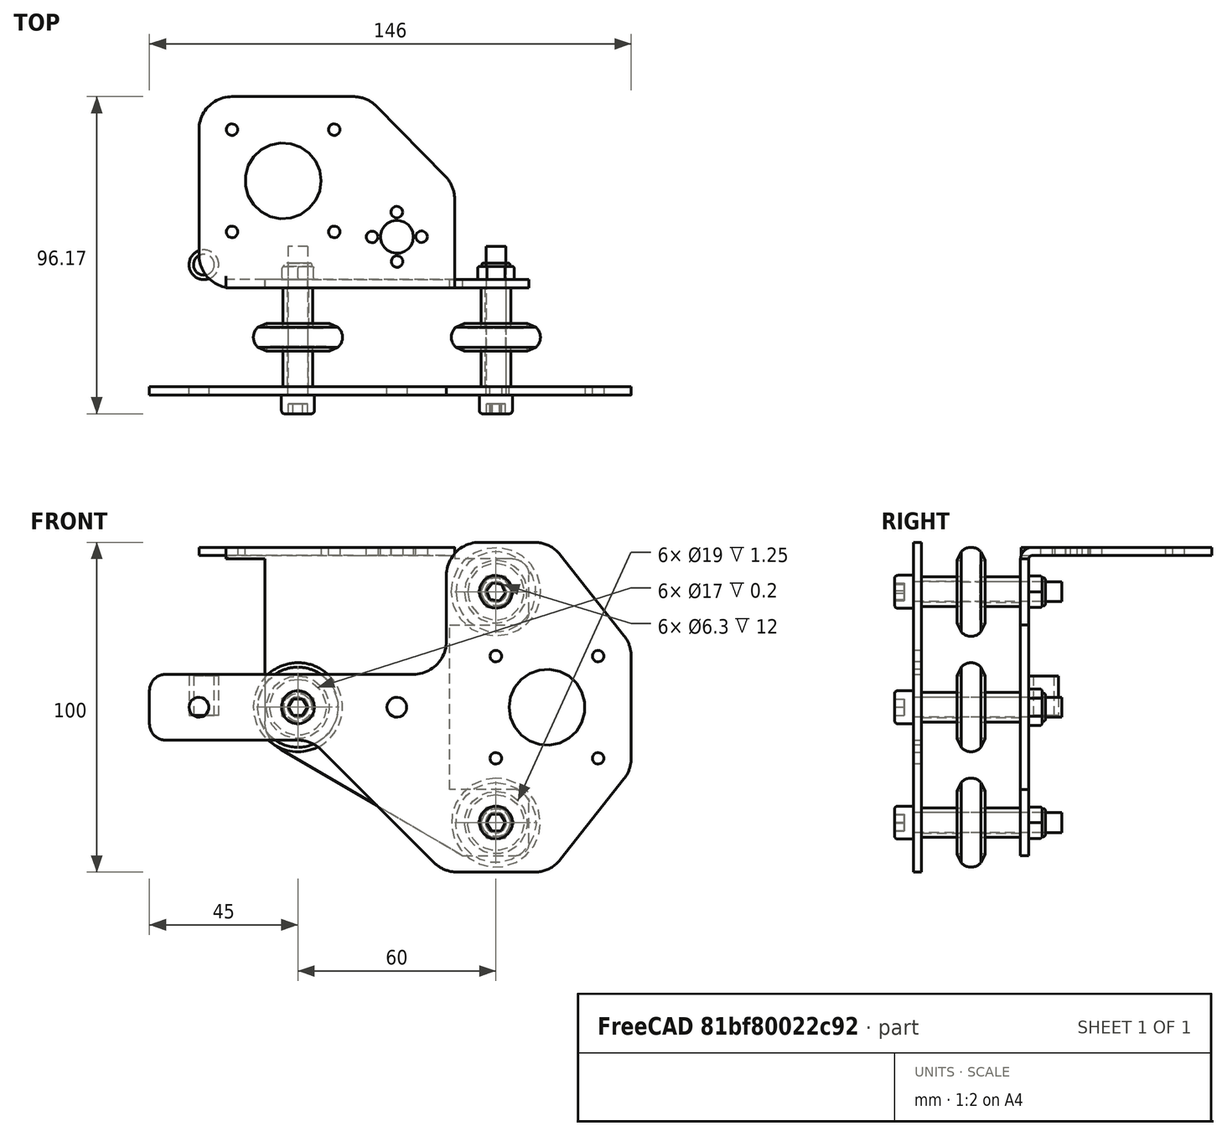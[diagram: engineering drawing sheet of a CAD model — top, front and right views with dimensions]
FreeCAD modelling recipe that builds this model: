
FCSTD DOCUMENT  (FreeCAD 0.19R24276 (Git))
Label: TESTE
License: All rights reserved
LicenseURL: http://en.wikipedia.org/wiki/All_rights_reserved
objects: App::FeaturePython×106, Part::FeaturePython×43, Part::Feature×17, Raytracing::RayFeature×17, App::Link×6, Sketcher::SketchObject×1, PartDesign::Pad×1, PartDesign::Body×1, Raytracing::RayProject×1
note: 63 computed .brp shape members not serialized (recipe doc carries the construction recipe); baked Part::Feature solids carry a one-line shape summary decoded from their .brp

FEATURE [Part::Feature] Part__Feature001  label="M6_locknut"
  Placement = pos=(88.5,-4.5,37.5) rot=(-1,0,0;1.5708rad)
  shape: bbox 11 x 5 x 9.526 mm, 25 faces (baked)
FEATURE [Part::Feature] Part__Feature002  label="Body001"
  Placement = pos=(104,-39.5,2.5) rot=(0,0.707107,0.707107;3.14159rad)
  shape: bbox 146 x 2.5 x 100 mm, 32 faces (baked)
FEATURE [Part::Feature] Part__Feature003  label="Body002"
  Placement = pos=(88.5,-6.99999,-32.5) rot=(0,0.707107,0.707107;3.14159rad)
  shape: bbox 100 x 57.97 x 93.5 mm, 48 faces (baked)
FEATURE [Part::Feature] Part__Feature004  label="VM8_R6x27x8.5"
  Placement = pos=(28.5,-22,2.5) rot=(-1,0,0;1.5708rad)
  shape: bbox 27 x 8.5 x 27 mm, 16 faces (baked)
FEATURE [Part::Feature] Part__Feature005  label="VM8_R6x27x8.5_2"
  Placement = pos=(88.5,-22,-32.5) rot=(-0.999999,-0.000736,-0.000736;1.5708rad)
  shape: bbox 27 x 8.5 x 27 mm, 16 faces (baked)
FEATURE [Part::Feature] Part__Feature006  label="VM8_R6x27x8.5_3"
  Placement = pos=(88.5,-22,37.5) rot=(0.577658,0.577197,-0.577196;2.09393rad)
  shape: bbox 27 x 8.5 x 27 mm, 16 faces (baked)
FEATURE [Part::Feature] Part__Feature009  label="M6_locknut001"
  Placement = pos=(88.5,-4.49999,-32.5) rot=(-1,0,0;1.5708rad)
  shape: bbox 11 x 5 x 9.526 mm, 25 faces (baked)
FEATURE [Part::Feature] Part__Feature010  label="M6_locknut002"
  Placement = pos=(28.5,-4.49999,2.50001) rot=(-0.935113,-0.250563,-0.250563;1.63783rad)
  shape: bbox 9.526 x 5 x 11 mm, 25 faces (baked)
FEATURE [Sketcher::SketchObject] Sketch
  FullyConstrained = true
  MapMode = 5
  Support = -> [XY_Plane]
  sketch-geometry (2):
    g0: Circle CenterX=0 CenterY=0 CenterZ=0 NormalX=0 NormalY=0 NormalZ=1 AngleXU=0 Radius=3.15
    g1: Circle CenterX=0 CenterY=0 CenterZ=0 NormalX=0 NormalY=0 NormalZ=1 AngleXU=0 Radius=4.5
  constraints (4):
    c: Coincident(g0,g-1)
    c: Coincident(g1,g0)
    c: Diameter(g0) = 6.3
    c: Diameter(g1) = 9
FEATURE [PartDesign::Pad] Pad
  Direction = (1,1,1)
  Length = 12
  Length2 = 100
  Profile = -> Sketch
  Type = 0
FEATURE [PartDesign::Body] Body  label="Spacer"
  Group = -> [Sketch,Pad]
  Origin = -> Origin
  Tip = -> Pad
FEATURE [App::Link] Link  label="Spacer001"
  LinkPlacement = pos=(88.5,-37,37.5) rot=(8.5e-05,0.707107,0.707107;3.14176rad)
  LinkedObject = -> Body
  Placement = pos=(88.5,-37,37.5) rot=(8.5e-05,0.707107,0.707107;3.14176rad)
FEATURE [App::Link] Link001  label="Spacer002"
  LinkPlacement = pos=(28.5,-6.99999,2.50001) rot=(1,0,0;1.5708rad)
  LinkedObject = -> Body
  Placement = pos=(28.5,-6.99999,2.50001) rot=(1,0,0;1.5708rad)
FEATURE [App::Link] Link002  label="Spacer003"
  LinkPlacement = pos=(88.5,-7,37.5) rot=(0.779842,0.442632,-0.442632;1.81694rad)
  LinkedObject = -> Body
  Placement = pos=(88.5,-7,37.5) rot=(0.779842,0.442632,-0.442632;1.81694rad)
FEATURE [App::Link] Link003  label="Spacer004"
  LinkPlacement = pos=(88.5,-6.99999,-32.5) rot=(0.705888,0.50086,-0.50086;1.91226rad)
  LinkedObject = -> Link002
  Placement = pos=(88.5,-6.99999,-32.5) rot=(0.705888,0.50086,-0.50086;1.91226rad)
FEATURE [App::Link] Link004  label="Spacer005"
  LinkPlacement = pos=(28.5,-25,2.5) rot=(-0.999419,-0.024107,0.024107;4.71181rad)
  LinkedObject = -> Link003
  Placement = pos=(28.5,-25,2.5) rot=(-0.999419,-0.024107,0.024107;4.71181rad)
FEATURE [App::Link] Link005  label="Spacer006"
  LinkPlacement = pos=(88.5,-25,-32.5) rot=(0.780405,0.442136,-0.442136;1.81624rad)
  LinkedObject = -> Link004
  Placement = pos=(88.5,-25,-32.5) rot=(0.780405,0.442136,-0.442136;1.81624rad)
FEATURE [Part::Feature] Part__Feature  label="M6x45_001"
  Placement = pos=(28.5,-45.2,2.5) rot=(-1,4.1e-05,4.1e-05;1.5708rad)
  shape: bbox 10.82 x 50.7 x 10.82 mm, 13 faces (baked)
FEATURE [Part::Feature] Part__Feature011  label="M6x45_002"
  Placement = pos=(88.5,-45.2,37.5) rot=(-0.995159,0.06949,0.06949;1.57565rad)
  shape: bbox 10.72 x 50.7 x 10.72 mm, 13 faces (baked)
FEATURE [Part::Feature] Part__Feature012  label="M6x45_003"
  Placement = pos=(88.5,-45.2,-32.5) rot=(-0.999312,-0.026231,-0.026231;1.57149rad)
  shape: bbox 10.81 x 50.7 x 10.81 mm, 13 faces (baked)
FEATURE [Part::FeaturePython] Parts  # WARN: FeaturePython — macro-defined, semantics opaque (R4)
  Group = -> [Part__Feature001,Part__Feature002,Part__Feature003,Part__Feature004,Part__Feature005,Part__Feature009,Part__Feature010,Link,Link001,Link002,Link003,Link004,Link005,Part__Feature006,Part__Feature,Part__Feature011,Part__Feature012]
  GroupMode = 0
FEATURE [Part::Feature] Link006  label="Spacer007"
  Placement = pos=(88.5,-37,37.5) rot=(8.5e-05,0.707107,0.707107;3.14176rad)
  shape: bbox 9 x 12 x 9 mm, 4 faces (baked)
FEATURE [Part::Feature] Link001001  label="Spacer008"
  Placement = pos=(28.5,-6.99999,2.50001) rot=(1,0,0;1.5708rad)
  shape: bbox 9 x 12 x 9 mm, 4 faces (baked)
FEATURE [Part::Feature] Link002001  label="Spacer009"
  Placement = pos=(88.5,-7,37.5) rot=(0.779842,0.442632,-0.442632;1.81694rad)
  shape: bbox 9 x 12 x 9 mm, 4 faces (baked)
FEATURE [Part::Feature] Link003001  label="Spacer010"
  Placement = pos=(88.5,-6.99999,-32.5) rot=(0.705888,0.50086,-0.50086;1.91226rad)
  shape: bbox 9 x 12 x 9 mm, 4 faces (baked)
FEATURE [Part::Feature] Link004001  label="Spacer011"
  Placement = pos=(28.5,-25,2.5) rot=(0.999419,0.024107,-0.024107;1.57138rad)
  shape: bbox 9 x 12 x 9 mm, 4 faces (baked)
FEATURE [Part::Feature] Link005001  label="Spacer012"
  Placement = pos=(88.5,-25,-32.5) rot=(0.780405,0.442136,-0.442136;1.81624rad)
  shape: bbox 9 x 12 x 9 mm, 4 faces (baked)
FEATURE [Raytracing::RayFeature] Part__Feature001_View
  Result = <blob: 83431 chars omitted>
  Source = -> Part__Feature001
  Transparency = 0
FEATURE [Raytracing::RayFeature] Part__Feature002_View
  Result = <blob: 113510 chars omitted>
  Source = -> Part__Feature002
  Transparency = 0
FEATURE [Raytracing::RayFeature] Part__Feature003_View
  Result = <blob: 158414 chars omitted>
  Source = -> Part__Feature003
  Transparency = 0
FEATURE [Raytracing::RayFeature] Part__Feature004_View
  Result = <blob: 100256 chars omitted>
  Source = -> Part__Feature004
  Transparency = 0
FEATURE [Raytracing::RayFeature] Part__Feature005_View
  Result = <blob: 101580 chars omitted>
  Source = -> Part__Feature005
  Transparency = 0
FEATURE [Raytracing::RayFeature] Part__Feature009_View
  Result = <blob: 84757 chars omitted>
  Source = -> Part__Feature009
  Transparency = 0
FEATURE [Raytracing::RayFeature] Part__Feature010_View
  Result = <blob: 84754 chars omitted>
  Source = -> Part__Feature010
  Transparency = 0
FEATURE [Raytracing::RayFeature] Part__Feature006_View
  Result = <blob: 100145 chars omitted>
  Source = -> Part__Feature006
  Transparency = 0
FEATURE [Raytracing::RayFeature] Part__Feature_View
  Result = <blob: 44517 chars omitted>
  Source = -> Part__Feature
  Transparency = 0
FEATURE [Raytracing::RayFeature] Part__Feature011_View
  Result = <blob: 44272 chars omitted>
  Source = -> Part__Feature011
  Transparency = 0
FEATURE [Raytracing::RayFeature] Part__Feature012_View
  Result = <blob: 44982 chars omitted>
  Source = -> Part__Feature012
  Transparency = 0
FEATURE [Raytracing::RayFeature] Link006_View
  Result = <blob: 19088 chars omitted>
  Source = -> Link006
  Transparency = 0
FEATURE [Raytracing::RayFeature] Link001001_View
  Result = <blob: 19740 chars omitted>
  Source = -> Link001001
  Transparency = 0
FEATURE [Raytracing::RayFeature] Link002001_View
  Result = <blob: 19164 chars omitted>
  Source = -> Link002001
  Transparency = 0
FEATURE [Raytracing::RayFeature] Link003001_View
  Result = <blob: 20088 chars omitted>
  Source = -> Link003001
  Transparency = 0
FEATURE [Raytracing::RayFeature] Link004001_View
  Result = <blob: 19376 chars omitted>
  Source = -> Link004001
  Transparency = 0
FEATURE [Raytracing::RayFeature] Link005001_View
  Result = <blob: 19390 chars omitted>
  Source = -> Link005001
  Transparency = 0
FEATURE [Raytracing::RayProject] PovProject
  Camera = // declares position and view direction\n\n// Generated by FreeCAD (http://www.freecadweb.org/)\n#declare cam_location =  <173.633,128.012,109.313>;\n#declare cam_look_at  = <37.8487,-7.77237,-26.4708>;\n#declare cam_sky      = <-0.408248,0.816496,-0.408249>;\n#declare cam_angle    = 45; \ncamera {\n  location  cam_location\n  look_at   cam_look_at\n  sky       cam_sky\n  angle     cam_angle \n  right x*800/600\n}
  Group = -> [Part__Feature001_View,Part__Feature002_View,Part__Feature003_View,Part__Feature004_View,Part__Feature005_View,Part__Feature009_View,Part__Feature010_View,Part__Feature006_View,Part__Feature_View,Part__Feature011_View,Part__Feature012_View,Link006_View,Link001001_View,Link002001_View,Link003001_View,Link004001_View,Link005001_View]
  Template = <path>
FEATURE [Part::FeaturePython] Assembly  # WARN: FeaturePython — macro-defined, semantics opaque (R4)
  AutoRelax = true
  BuildShape = 0
  Freeze = false
  Group = -> [Constraints,Elements,Parts]
  Verbose = false
  _SolverType = 1
  _Version = 1
FEATURE [App::FeaturePython] Constraints  # WARN: FeaturePython — macro-defined, semantics opaque (R4)
  Group = -> [Constraint,Constraint001,Constraint002,Constraint003,Constraint004,Constraint005,Constraint006,Constraint007,Constraint008,Constraint009,Constraint010,Constraint011,Constraint012,Constraint013,Constraint014,Constraint015,Constraint016,Constraint017,Constraint018,Constraint019,Constraint020,Constraint021,Constraint022,Constraint023,Constraint024,Constraint025,Constraint026,Constraint027,+7 more]
  _Version = 1
FEATURE [App::FeaturePython] Elements  # WARN: FeaturePython — macro-defined, semantics opaque (R4)
  Group = -> [_Element,_Element001,_Element002,_Element003,_Element004,_Element005,_Element006,_Element007,_Element008,_Element009,_Element010,_Element011,_Element012,_Element013,_Element014,_Element015,_Element016,_Element017,_Element018,_Element019,_Element020,_Element021,_Element022,_Element023,_Element024,_Element025,_Element026,_Element027,_Element028,_Element029,_Element030,_Element031,_Element032,+8 more]
FEATURE [App::FeaturePython] Constraint  label="AxialAlignment"  # WARN: FeaturePython — macro-defined, semantics opaque (R4)
  Angle = 0
  AnglePitch = 0
  AngleRoll = 0
  Disabled = false
  Group = -> [ElementLink,ElementLink001]
  LockAngle = false
  Multiply = false
  _ConstraintType = 36
  _Parent = -> Constraints
FEATURE [App::FeaturePython] ElementLink  label="_Element"  # link proxy (typed FeaturePython)
  LinkTransform = true
  LinkedObject = -> _Element
  _Parent = -> Constraint
FEATURE [Part::FeaturePython] _Element  # link proxy (typed FeaturePython)
  Detach = false
  LinkTransform = true
  LinkedObject = -> Part__Feature002 [Edge69]
  _Parent = -> Elements
FEATURE [App::FeaturePython] ElementLink001  label="_Element001"  # link proxy (typed FeaturePython)
  LinkTransform = true
  LinkedObject = -> _Element001
  _Parent = -> Constraint
FEATURE [Part::FeaturePython] _Element001  # link proxy (typed FeaturePython)
  Detach = false
  LinkTransform = true
  LinkedObject = -> Part__Feature011 [Edge14]
  _Parent = -> Elements
FEATURE [App::FeaturePython] Constraint001  label="Locked"  # WARN: FeaturePython — macro-defined, semantics opaque (R4)
  Disabled = false
  Group = -> [ElementLink002]
  _ConstraintType = 0
  _Parent = -> Constraints
FEATURE [App::FeaturePython] ElementLink002  label="_Element002"  # link proxy (typed FeaturePython)
  LinkTransform = true
  LinkedObject = -> _Element002
  _Parent = -> Constraint001
FEATURE [Part::FeaturePython] _Element002  # link proxy (typed FeaturePython)
  Detach = false
  LinkTransform = true
  LinkedObject = -> Part__Feature002 [Face32]
  _Parent = -> Elements
FEATURE [App::FeaturePython] Constraint002  label="AxialAlignment001"  # WARN: FeaturePython — macro-defined, semantics opaque (R4)
  Angle = 0
  AnglePitch = 0
  AngleRoll = 0
  Disabled = false
  Group = -> [ElementLink003,ElementLink004]
  LockAngle = false
  Multiply = false
  _ConstraintType = 36
  _Parent = -> Constraints
FEATURE [App::FeaturePython] ElementLink003  label="_Element003"  # link proxy (typed FeaturePython)
  LinkTransform = true
  LinkedObject = -> _Element003
  _Parent = -> Constraint002
FEATURE [Part::FeaturePython] _Element003  # link proxy (typed FeaturePython)
  Detach = false
  LinkTransform = true
  LinkedObject = -> Part__Feature002 [Edge75]
  _Parent = -> Elements
FEATURE [App::FeaturePython] ElementLink004  label="_Element004"  # link proxy (typed FeaturePython)
  LinkTransform = true
  LinkedObject = -> _Element004
  _Parent = -> Constraint002
FEATURE [Part::FeaturePython] _Element004  # link proxy (typed FeaturePython)
  Detach = false
  LinkTransform = true
  LinkedObject = -> Part__Feature [Edge14]
  _Parent = -> Elements
FEATURE [App::FeaturePython] Constraint003  label="AxialAlignment002"  # WARN: FeaturePython — macro-defined, semantics opaque (R4)
  Angle = 0
  AnglePitch = 0
  AngleRoll = 0
  Disabled = false
  Group = -> [ElementLink005,ElementLink006]
  LockAngle = false
  Multiply = false
  _ConstraintType = 36
  _Parent = -> Constraints
FEATURE [App::FeaturePython] ElementLink005  label="_Element005"  # link proxy (typed FeaturePython)
  LinkTransform = true
  LinkedObject = -> _Element005
  _Parent = -> Constraint003
FEATURE [Part::FeaturePython] _Element005  # link proxy (typed FeaturePython)
  Detach = false
  LinkTransform = true
  LinkedObject = -> Part__Feature012 [Edge14]
  _Parent = -> Elements
FEATURE [App::FeaturePython] ElementLink006  label="_Element006"  # link proxy (typed FeaturePython)
  LinkTransform = true
  LinkedObject = -> _Element006
  _Parent = -> Constraint003
FEATURE [Part::FeaturePython] _Element006  # link proxy (typed FeaturePython)
  Detach = false
  LinkTransform = true
  LinkedObject = -> Part__Feature002 [Edge66]
  _Parent = -> Elements
FEATURE [App::FeaturePython] Constraint004  label="PointsCoincident"  # WARN: FeaturePython — macro-defined, semantics opaque (R4)
  Disabled = false
  Group = -> [ElementLink007,ElementLink008]
  _ConstraintType = 1
  _Parent = -> Constraints
FEATURE [App::FeaturePython] ElementLink007  label="_Element007"  # link proxy (typed FeaturePython)
  LinkTransform = true
  LinkedObject = -> _Element007
  _Parent = -> Constraint004
FEATURE [Part::FeaturePython] _Element007  # link proxy (typed FeaturePython)
  Detach = false
  LinkTransform = true
  LinkedObject = -> Part__Feature012 [Edge6]
  _Parent = -> Elements
FEATURE [App::FeaturePython] ElementLink008  label="_Element008"  # link proxy (typed FeaturePython)
  LinkTransform = true
  LinkedObject = -> _Element008
  _Parent = -> Constraint004
FEATURE [Part::FeaturePython] _Element008  # link proxy (typed FeaturePython)
  Detach = false
  LinkTransform = true
  LinkedObject = -> Part__Feature002 [Edge64]
  _Parent = -> Elements
FEATURE [App::FeaturePython] Constraint005  label="PointsCoincident001"  # WARN: FeaturePython — macro-defined, semantics opaque (R4)
  Disabled = false
  Group = -> [ElementLink009,ElementLink010]
  _ConstraintType = 1
  _Parent = -> Constraints
FEATURE [App::FeaturePython] ElementLink009  label="_Element009"  # link proxy (typed FeaturePython)
  LinkTransform = true
  LinkedObject = -> _Element009
  _Parent = -> Constraint005
FEATURE [Part::FeaturePython] _Element009  # link proxy (typed FeaturePython)
  Detach = false
  LinkTransform = true
  LinkedObject = -> Part__Feature002 [Edge67]
  _Parent = -> Elements
FEATURE [App::FeaturePython] ElementLink010  label="_Element010"  # link proxy (typed FeaturePython)
  LinkTransform = true
  LinkedObject = -> _Element010
  _Parent = -> Constraint005
FEATURE [Part::FeaturePython] _Element010  # link proxy (typed FeaturePython)
  Detach = false
  LinkTransform = true
  LinkedObject = -> Part__Feature011 [Edge6]
  _Parent = -> Elements
FEATURE [App::FeaturePython] Constraint006  label="PointsCoincident002"  # WARN: FeaturePython — macro-defined, semantics opaque (R4)
  Disabled = false
  Group = -> [ElementLink011,ElementLink012]
  _ConstraintType = 1
  _Parent = -> Constraints
FEATURE [App::FeaturePython] ElementLink011  label="_Element011"  # link proxy (typed FeaturePython)
  LinkTransform = true
  LinkedObject = -> _Element011
  _Parent = -> Constraint006
FEATURE [Part::FeaturePython] _Element011  # link proxy (typed FeaturePython)
  Detach = false
  LinkTransform = true
  LinkedObject = -> Part__Feature002 [Edge73]
  _Parent = -> Elements
FEATURE [App::FeaturePython] ElementLink012  label="_Element012"  # link proxy (typed FeaturePython)
  LinkTransform = true
  LinkedObject = -> _Element012
  _Parent = -> Constraint006
FEATURE [Part::FeaturePython] _Element012  # link proxy (typed FeaturePython)
  Detach = false
  LinkTransform = true
  LinkedObject = -> Part__Feature [Edge6]
  _Parent = -> Elements
FEATURE [App::FeaturePython] Constraint007  label="PointsCoincident003"  # WARN: FeaturePython — macro-defined, semantics opaque (R4)
  Disabled = false
  Group = -> [ElementLink013,ElementLink014]
  _ConstraintType = 1
  _Parent = -> Constraints
FEATURE [App::FeaturePython] ElementLink013  label="_Element013"  # link proxy (typed FeaturePython)
  LinkTransform = true
  LinkedObject = -> _Element013
  _Parent = -> Constraint007
FEATURE [Part::FeaturePython] _Element013  # link proxy (typed FeaturePython)
  Detach = false
  LinkTransform = true
  LinkedObject = -> Link [Pad.Edge5]
  _Parent = -> Elements
FEATURE [App::FeaturePython] ElementLink014  label="_Element"  # link proxy (typed FeaturePython)
  LinkTransform = true
  LinkedObject = -> _Element
  _Parent = -> Constraint007
FEATURE [App::FeaturePython] Constraint008  label="AxialAlignment003"  # WARN: FeaturePython — macro-defined, semantics opaque (R4)
  Angle = 0
  AnglePitch = 0
  AngleRoll = 0
  Disabled = false
  Group = -> [ElementLink015,ElementLink016]
  LockAngle = false
  Multiply = false
  _ConstraintType = 36
  _Parent = -> Constraints
FEATURE [App::FeaturePython] ElementLink015  label="_Element014"  # link proxy (typed FeaturePython)
  LinkTransform = true
  LinkedObject = -> _Element014
  _Parent = -> Constraint008
FEATURE [Part::FeaturePython] _Element014  # link proxy (typed FeaturePython)
  Detach = false
  LinkTransform = true
  LinkedObject = -> Link [Pad.Edge6]
  _Parent = -> Elements
FEATURE [App::FeaturePython] ElementLink016  label="_Element001"  # link proxy (typed FeaturePython)
  LinkTransform = true
  LinkedObject = -> _Element001
  _Parent = -> Constraint008
FEATURE [App::FeaturePython] Constraint009  label="PointsCoincident004"  # WARN: FeaturePython — macro-defined, semantics opaque (R4)
  Disabled = false
  Group = -> [ElementLink017,ElementLink018]
  _ConstraintType = 1
  _Parent = -> Constraints
FEATURE [App::FeaturePython] ElementLink017  label="_Element015"  # link proxy (typed FeaturePython)
  LinkTransform = true
  LinkedObject = -> _Element015
  _Parent = -> Constraint009
FEATURE [Part::FeaturePython] _Element015  # link proxy (typed FeaturePython)
  Detach = false
  LinkTransform = true
  LinkedObject = -> Link004 [Pad.Edge6]
  _Parent = -> Elements
FEATURE [App::FeaturePython] ElementLink018  label="_Element003"  # link proxy (typed FeaturePython)
  LinkTransform = true
  LinkedObject = -> _Element003
  _Parent = -> Constraint009
FEATURE [App::FeaturePython] Constraint010  label="AxialAlignment004"  # WARN: FeaturePython — macro-defined, semantics opaque (R4)
  Angle = 0
  AnglePitch = 0
  AngleRoll = 0
  Disabled = false
  Group = -> [ElementLink019,ElementLink020]
  LockAngle = false
  Multiply = false
  _ConstraintType = 36
  _Parent = -> Constraints
FEATURE [App::FeaturePython] ElementLink019  label="_Element016"  # link proxy (typed FeaturePython)
  LinkTransform = true
  LinkedObject = -> _Element016
  _Parent = -> Constraint010
FEATURE [Part::FeaturePython] _Element016  # link proxy (typed FeaturePython)
  Detach = false
  LinkTransform = true
  LinkedObject = -> Link004 [Pad.Edge5]
  _Parent = -> Elements
FEATURE [App::FeaturePython] ElementLink020  label="_Element004"  # link proxy (typed FeaturePython)
  LinkTransform = true
  LinkedObject = -> _Element004
  _Parent = -> Constraint010
FEATURE [App::FeaturePython] Constraint011  label="PointsCoincident005"  # WARN: FeaturePython — macro-defined, semantics opaque (R4)
  Disabled = false
  Group = -> [ElementLink021,ElementLink022]
  _ConstraintType = 1
  _Parent = -> Constraints
FEATURE [App::FeaturePython] ElementLink021  label="_Element017"  # link proxy (typed FeaturePython)
  LinkTransform = true
  LinkedObject = -> _Element017
  _Parent = -> Constraint011
FEATURE [Part::FeaturePython] _Element017  # link proxy (typed FeaturePython)
  Detach = false
  LinkTransform = true
  LinkedObject = -> Link005 [Pad.Edge6]
  _Parent = -> Elements
FEATURE [App::FeaturePython] ElementLink022  label="_Element006"  # link proxy (typed FeaturePython)
  LinkTransform = true
  LinkedObject = -> _Element006
  _Parent = -> Constraint011
FEATURE [App::FeaturePython] Constraint012  label="AxialAlignment005"  # WARN: FeaturePython — macro-defined, semantics opaque (R4)
  Angle = 0
  AnglePitch = 0
  AngleRoll = 0
  Disabled = false
  Group = -> [ElementLink023,ElementLink024]
  LockAngle = false
  Multiply = false
  _ConstraintType = 36
  _Parent = -> Constraints
FEATURE [App::FeaturePython] ElementLink023  label="_Element018"  # link proxy (typed FeaturePython)
  LinkTransform = true
  LinkedObject = -> _Element018
  _Parent = -> Constraint012
FEATURE [Part::FeaturePython] _Element018  # link proxy (typed FeaturePython)
  Detach = false
  LinkTransform = true
  LinkedObject = -> Link005 [Pad.Edge5]
  _Parent = -> Elements
FEATURE [App::FeaturePython] ElementLink024  label="_Element005"  # link proxy (typed FeaturePython)
  LinkTransform = true
  LinkedObject = -> _Element005
  _Parent = -> Constraint012
FEATURE [App::FeaturePython] Constraint013  label="AxialAlignment006"  # WARN: FeaturePython — macro-defined, semantics opaque (R4)
  Angle = 0
  AnglePitch = 0
  AngleRoll = 0
  Disabled = false
  Group = -> [ElementLink025,ElementLink026]
  LockAngle = false
  Multiply = false
  _ConstraintType = 36
  _Parent = -> Constraints
FEATURE [App::FeaturePython] ElementLink025  label="_Element019"  # link proxy (typed FeaturePython)
  LinkTransform = true
  LinkedObject = -> _Element019
  _Parent = -> Constraint013
FEATURE [Part::FeaturePython] _Element019  # link proxy (typed FeaturePython)
  Detach = false
  LinkTransform = true
  LinkedObject = -> Part__Feature006 [Edge18]
  _Parent = -> Elements
FEATURE [App::FeaturePython] ElementLink026  label="_Element001"  # link proxy (typed FeaturePython)
  LinkTransform = true
  LinkedObject = -> _Element001
  _Parent = -> Constraint013
FEATURE [App::FeaturePython] Constraint014  label="PointsCoincident006"  # WARN: FeaturePython — macro-defined, semantics opaque (R4)
  Disabled = false
  Group = -> [ElementLink027,ElementLink028]
  _ConstraintType = 1
  _Parent = -> Constraints
FEATURE [App::FeaturePython] ElementLink027  label="_Element020"  # link proxy (typed FeaturePython)
  LinkTransform = true
  LinkedObject = -> _Element020
  _Parent = -> Constraint014
FEATURE [Part::FeaturePython] _Element020  # link proxy (typed FeaturePython)
  Detach = false
  LinkTransform = true
  LinkedObject = -> Part__Feature006 [Edge16]
  _Parent = -> Elements
FEATURE [App::FeaturePython] ElementLink028  label="_Element014"  # link proxy (typed FeaturePython)
  LinkTransform = true
  LinkedObject = -> _Element014
  _Parent = -> Constraint014
FEATURE [App::FeaturePython] Constraint015  label="AxialAlignment007"  # WARN: FeaturePython — macro-defined, semantics opaque (R4)
  Angle = 0
  AnglePitch = 0
  AngleRoll = 0
  Disabled = false
  Group = -> [ElementLink029,ElementLink030]
  LockAngle = false
  Multiply = false
  _ConstraintType = 36
  _Parent = -> Constraints
FEATURE [App::FeaturePython] ElementLink029  label="_Element021"  # link proxy (typed FeaturePython)
  LinkTransform = true
  LinkedObject = -> _Element021
  _Parent = -> Constraint015
FEATURE [Part::FeaturePython] _Element021  # link proxy (typed FeaturePython)
  Detach = false
  LinkTransform = true
  LinkedObject = -> Part__Feature004 [Edge16]
  _Parent = -> Elements
FEATURE [App::FeaturePython] ElementLink030  label="_Element004"  # link proxy (typed FeaturePython)
  LinkTransform = true
  LinkedObject = -> _Element004
  _Parent = -> Constraint015
FEATURE [App::FeaturePython] Constraint016  label="PointsCoincident007"  # WARN: FeaturePython — macro-defined, semantics opaque (R4)
  Disabled = false
  Group = -> [ElementLink031,ElementLink032]
  _ConstraintType = 1
  _Parent = -> Constraints
FEATURE [App::FeaturePython] ElementLink031  label="_Element022"  # link proxy (typed FeaturePython)
  LinkTransform = true
  LinkedObject = -> _Element022
  _Parent = -> Constraint016
FEATURE [Part::FeaturePython] _Element022  # link proxy (typed FeaturePython)
  Detach = false
  LinkTransform = true
  LinkedObject = -> Part__Feature004 [Edge18]
  _Parent = -> Elements
FEATURE [App::FeaturePython] ElementLink032  label="_Element016"  # link proxy (typed FeaturePython)
  LinkTransform = true
  LinkedObject = -> _Element016
  _Parent = -> Constraint016
FEATURE [App::FeaturePython] Constraint017  label="AxialAlignment008"  # WARN: FeaturePython — macro-defined, semantics opaque (R4)
  Angle = 0
  AnglePitch = 0
  AngleRoll = 0
  Disabled = false
  Group = -> [ElementLink033,ElementLink034]
  LockAngle = false
  Multiply = false
  _ConstraintType = 36
  _Parent = -> Constraints
FEATURE [App::FeaturePython] ElementLink033  label="_Element023"  # link proxy (typed FeaturePython)
  LinkTransform = true
  LinkedObject = -> _Element023
  _Parent = -> Constraint017
FEATURE [Part::FeaturePython] _Element023  # link proxy (typed FeaturePython)
  Detach = false
  LinkTransform = true
  LinkedObject = -> Part__Feature005 [Edge16]
  _Parent = -> Elements
FEATURE [App::FeaturePython] ElementLink034  label="_Element005"  # link proxy (typed FeaturePython)
  LinkTransform = true
  LinkedObject = -> _Element005
  _Parent = -> Constraint017
FEATURE [App::FeaturePython] Constraint018  label="PointsCoincident008"  # WARN: FeaturePython — macro-defined, semantics opaque (R4)
  Disabled = false
  Group = -> [ElementLink035,ElementLink036]
  _ConstraintType = 1
  _Parent = -> Constraints
FEATURE [App::FeaturePython] ElementLink035  label="_Element024"  # link proxy (typed FeaturePython)
  LinkTransform = true
  LinkedObject = -> _Element024
  _Parent = -> Constraint018
FEATURE [Part::FeaturePython] _Element024  # link proxy (typed FeaturePython)
  Detach = false
  LinkTransform = true
  LinkedObject = -> Part__Feature005 [Edge18]
  _Parent = -> Elements
FEATURE [App::FeaturePython] ElementLink036  label="_Element018"  # link proxy (typed FeaturePython)
  LinkTransform = true
  LinkedObject = -> _Element018
  _Parent = -> Constraint018
FEATURE [App::FeaturePython] Constraint019  label="AxialAlignment009"  # WARN: FeaturePython — macro-defined, semantics opaque (R4)
  Angle = 0
  AnglePitch = 0
  AngleRoll = 0
  Disabled = false
  Group = -> [ElementLink037,ElementLink038]
  LockAngle = false
  Multiply = false
  _ConstraintType = 36
  _Parent = -> Constraints
FEATURE [App::FeaturePython] ElementLink037  label="_Element025"  # link proxy (typed FeaturePython)
  LinkTransform = true
  LinkedObject = -> _Element025
  _Parent = -> Constraint019
FEATURE [Part::FeaturePython] _Element025  # link proxy (typed FeaturePython)
  Detach = false
  LinkTransform = true
  LinkedObject = -> Link001 [Pad.Edge5]
  _Parent = -> Elements
FEATURE [App::FeaturePython] ElementLink038  label="_Element004"  # link proxy (typed FeaturePython)
  LinkTransform = true
  LinkedObject = -> _Element004
  _Parent = -> Constraint019
FEATURE [App::FeaturePython] Constraint020  label="PointsCoincident009"  # WARN: FeaturePython — macro-defined, semantics opaque (R4)
  Disabled = false
  Group = -> [ElementLink039,ElementLink040]
  _ConstraintType = 1
  _Parent = -> Constraints
FEATURE [App::FeaturePython] ElementLink039  label="_Element026"  # link proxy (typed FeaturePython)
  LinkTransform = true
  LinkedObject = -> _Element026
  _Parent = -> Constraint020
FEATURE [Part::FeaturePython] _Element026  # link proxy (typed FeaturePython)
  Detach = false
  LinkTransform = true
  LinkedObject = -> Link001 [Pad.Edge6]
  _Parent = -> Elements
FEATURE [App::FeaturePython] ElementLink040  label="_Element021"  # link proxy (typed FeaturePython)
  LinkTransform = true
  LinkedObject = -> _Element021
  _Parent = -> Constraint020
FEATURE [App::FeaturePython] Constraint021  label="AxialAlignment010"  # WARN: FeaturePython — macro-defined, semantics opaque (R4)
  Angle = 0
  AnglePitch = 0
  AngleRoll = 0
  Disabled = false
  Group = -> [ElementLink041,ElementLink042]
  LockAngle = false
  Multiply = false
  _ConstraintType = 36
  _Parent = -> Constraints
FEATURE [App::FeaturePython] ElementLink041  label="_Element027"  # link proxy (typed FeaturePython)
  LinkTransform = true
  LinkedObject = -> _Element027
  _Parent = -> Constraint021
FEATURE [Part::FeaturePython] _Element027  # link proxy (typed FeaturePython)
  Detach = false
  LinkTransform = true
  LinkedObject = -> Link002 [Pad.Edge5]
  _Parent = -> Elements
FEATURE [App::FeaturePython] ElementLink042  label="_Element001"  # link proxy (typed FeaturePython)
  LinkTransform = true
  LinkedObject = -> _Element001
  _Parent = -> Constraint021
FEATURE [App::FeaturePython] Constraint022  label="PointsCoincident010"  # WARN: FeaturePython — macro-defined, semantics opaque (R4)
  Disabled = false
  Group = -> [ElementLink043,ElementLink044]
  _ConstraintType = 1
  _Parent = -> Constraints
FEATURE [App::FeaturePython] ElementLink043  label="_Element028"  # link proxy (typed FeaturePython)
  LinkTransform = true
  LinkedObject = -> _Element028
  _Parent = -> Constraint022
FEATURE [Part::FeaturePython] _Element028  # link proxy (typed FeaturePython)
  Detach = false
  LinkTransform = true
  LinkedObject = -> Link002 [Pad.Edge6]
  _Parent = -> Elements
FEATURE [App::FeaturePython] ElementLink044  label="_Element019"  # link proxy (typed FeaturePython)
  LinkTransform = true
  LinkedObject = -> _Element019
  _Parent = -> Constraint022
FEATURE [App::FeaturePython] Constraint023  label="PointsCoincident011"  # WARN: FeaturePython — macro-defined, semantics opaque (R4)
  Disabled = false
  Group = -> [ElementLink045,ElementLink046]
  _ConstraintType = 1
  _Parent = -> Constraints
FEATURE [App::FeaturePython] ElementLink045  label="_Element029"  # link proxy (typed FeaturePython)
  LinkTransform = true
  LinkedObject = -> _Element029
  _Parent = -> Constraint023
FEATURE [Part::FeaturePython] _Element029  # link proxy (typed FeaturePython)
  Detach = false
  LinkTransform = true
  LinkedObject = -> Link003 [Pad.Edge6]
  _Parent = -> Elements
FEATURE [App::FeaturePython] ElementLink046  label="_Element023"  # link proxy (typed FeaturePython)
  LinkTransform = true
  LinkedObject = -> _Element023
  _Parent = -> Constraint023
FEATURE [App::FeaturePython] Constraint024  label="AxialAlignment011"  # WARN: FeaturePython — macro-defined, semantics opaque (R4)
  Angle = 0
  AnglePitch = 0
  AngleRoll = 0
  Disabled = false
  Group = -> [ElementLink047,ElementLink048]
  LockAngle = false
  Multiply = false
  _ConstraintType = 36
  _Parent = -> Constraints
FEATURE [App::FeaturePython] ElementLink047  label="_Element030"  # link proxy (typed FeaturePython)
  LinkTransform = true
  LinkedObject = -> _Element030
  _Parent = -> Constraint024
FEATURE [Part::FeaturePython] _Element030  # link proxy (typed FeaturePython)
  Detach = false
  LinkTransform = true
  LinkedObject = -> Link003 [Pad.Edge5]
  _Parent = -> Elements
FEATURE [App::FeaturePython] ElementLink048  label="_Element005"  # link proxy (typed FeaturePython)
  LinkTransform = true
  LinkedObject = -> _Element005
  _Parent = -> Constraint024
FEATURE [App::FeaturePython] Constraint025  label="AxialAlignment012"  # WARN: FeaturePython — macro-defined, semantics opaque (R4)
  Angle = 0
  AnglePitch = 0
  AngleRoll = 0
  Disabled = false
  Group = -> [ElementLink049,ElementLink050]
  LockAngle = false
  Multiply = false
  _ConstraintType = 36
  _Parent = -> Constraints
FEATURE [App::FeaturePython] ElementLink049  label="_Element031"  # link proxy (typed FeaturePython)
  LinkTransform = true
  LinkedObject = -> _Element031
  _Parent = -> Constraint025
FEATURE [Part::FeaturePython] _Element031  # link proxy (typed FeaturePython)
  Detach = false
  LinkTransform = true
  LinkedObject = -> Part__Feature003 [Edge28]
  _Parent = -> Elements
FEATURE [App::FeaturePython] ElementLink050  label="_Element001"  # link proxy (typed FeaturePython)
  LinkTransform = true
  LinkedObject = -> _Element001
  _Parent = -> Constraint025
FEATURE [App::FeaturePython] Constraint026  label="AxialAlignment013"  # WARN: FeaturePython — macro-defined, semantics opaque (R4)
  Angle = 0
  AnglePitch = 0
  AngleRoll = 0
  Disabled = false
  Group = -> [ElementLink051,ElementLink052]
  LockAngle = false
  Multiply = false
  _ConstraintType = 36
  _Parent = -> Constraints
FEATURE [App::FeaturePython] ElementLink051  label="_Element032"  # link proxy (typed FeaturePython)
  LinkTransform = true
  LinkedObject = -> _Element032
  _Parent = -> Constraint026
FEATURE [Part::FeaturePython] _Element032  # link proxy (typed FeaturePython)
  Detach = false
  LinkTransform = true
  LinkedObject = -> Part__Feature003 [Edge27]
  _Parent = -> Elements
FEATURE [App::FeaturePython] ElementLink052  label="_Element005"  # link proxy (typed FeaturePython)
  LinkTransform = true
  LinkedObject = -> _Element005
  _Parent = -> Constraint026
FEATURE [App::FeaturePython] Constraint027  label="AxialAlignment014"  # WARN: FeaturePython — macro-defined, semantics opaque (R4)
  Angle = 0
  AnglePitch = 0
  AngleRoll = 0
  Disabled = false
  Group = -> [ElementLink053,ElementLink054]
  LockAngle = false
  Multiply = false
  _ConstraintType = 36
  _Parent = -> Constraints
FEATURE [App::FeaturePython] ElementLink053  label="_Element033"  # link proxy (typed FeaturePython)
  LinkTransform = true
  LinkedObject = -> _Element033
  _Parent = -> Constraint027
FEATURE [Part::FeaturePython] _Element033  # link proxy (typed FeaturePython)
  Detach = false
  LinkTransform = true
  LinkedObject = -> Part__Feature003 [Edge26]
  _Parent = -> Elements
FEATURE [App::FeaturePython] ElementLink054  label="_Element004"  # link proxy (typed FeaturePython)
  LinkTransform = true
  LinkedObject = -> _Element004
  _Parent = -> Constraint027
FEATURE [App::FeaturePython] Constraint028  label="PointsCoincident012"  # WARN: FeaturePython — macro-defined, semantics opaque (R4)
  Disabled = false
  Group = -> [ElementLink055,ElementLink056]
  _ConstraintType = 1
  _Parent = -> Constraints
FEATURE [App::FeaturePython] ElementLink055  label="_Element025"  # link proxy (typed FeaturePython)
  LinkTransform = true
  LinkedObject = -> _Element025
  _Parent = -> Constraint028
FEATURE [App::FeaturePython] ElementLink056  label="_Element034"  # link proxy (typed FeaturePython)
  LinkTransform = true
  LinkedObject = -> _Element034
  _Parent = -> Constraint028
FEATURE [Part::FeaturePython] _Element034  # link proxy (typed FeaturePython)
  Detach = false
  LinkTransform = true
  LinkedObject = -> Part__Feature003 [Edge90]
  _Parent = -> Elements
FEATURE [App::FeaturePython] Constraint029  label="AxialAlignment015"  # WARN: FeaturePython — macro-defined, semantics opaque (R4)
  Angle = 0
  AnglePitch = 0
  AngleRoll = 0
  Disabled = false
  Group = -> [ElementLink057,ElementLink058]
  LockAngle = false
  Multiply = false
  _ConstraintType = 36
  _Parent = -> Constraints
FEATURE [App::FeaturePython] ElementLink057  label="_Element035"  # link proxy (typed FeaturePython)
  LinkTransform = true
  LinkedObject = -> _Element035
  _Parent = -> Constraint029
FEATURE [Part::FeaturePython] _Element035  # link proxy (typed FeaturePython)
  Detach = false
  LinkTransform = true
  LinkedObject = -> Part__Feature001 [Edge50]
  _Parent = -> Elements
FEATURE [App::FeaturePython] ElementLink058  label="_Element001"  # link proxy (typed FeaturePython)
  LinkTransform = true
  LinkedObject = -> _Element001
  _Parent = -> Constraint029
FEATURE [App::FeaturePython] Constraint030  label="PointsCoincident013"  # WARN: FeaturePython — macro-defined, semantics opaque (R4)
  Disabled = false
  Group = -> [ElementLink059,ElementLink060]
  _ConstraintType = 1
  _Parent = -> Constraints
FEATURE [App::FeaturePython] ElementLink059  label="_Element031"  # link proxy (typed FeaturePython)
  LinkTransform = true
  LinkedObject = -> _Element031
  _Parent = -> Constraint030
FEATURE [App::FeaturePython] ElementLink060  label="_Element036"  # link proxy (typed FeaturePython)
  LinkTransform = true
  LinkedObject = -> _Element036
  _Parent = -> Constraint030
FEATURE [Part::FeaturePython] _Element036  # link proxy (typed FeaturePython)
  Detach = false
  LinkTransform = true
  LinkedObject = -> Part__Feature001 [Edge28]
  _Parent = -> Elements
FEATURE [App::FeaturePython] Constraint031  label="AxialAlignment016"  # WARN: FeaturePython — macro-defined, semantics opaque (R4)
  Angle = 0
  AnglePitch = 0
  AngleRoll = 0
  Disabled = false
  Group = -> [ElementLink061,ElementLink062]
  LockAngle = false
  Multiply = false
  _ConstraintType = 36
  _Parent = -> Constraints
FEATURE [App::FeaturePython] ElementLink061  label="_Element037"  # link proxy (typed FeaturePython)
  LinkTransform = true
  LinkedObject = -> _Element037
  _Parent = -> Constraint031
FEATURE [Part::FeaturePython] _Element037  # link proxy (typed FeaturePython)
  Detach = false
  LinkTransform = true
  LinkedObject = -> Part__Feature009 [Edge50]
  _Parent = -> Elements
FEATURE [App::FeaturePython] ElementLink062  label="_Element005"  # link proxy (typed FeaturePython)
  LinkTransform = true
  LinkedObject = -> _Element005
  _Parent = -> Constraint031
FEATURE [App::FeaturePython] Constraint032  label="PointsCoincident014"  # WARN: FeaturePython — macro-defined, semantics opaque (R4)
  Disabled = false
  Group = -> [ElementLink063,ElementLink064]
  _ConstraintType = 1
  _Parent = -> Constraints
FEATURE [App::FeaturePython] ElementLink063  label="_Element038"  # link proxy (typed FeaturePython)
  LinkTransform = true
  LinkedObject = -> _Element038
  _Parent = -> Constraint032
FEATURE [Part::FeaturePython] _Element038  # link proxy (typed FeaturePython)
  Detach = false
  LinkTransform = true
  LinkedObject = -> Part__Feature009 [Edge28]
  _Parent = -> Elements
FEATURE [App::FeaturePython] ElementLink064  label="_Element032"  # link proxy (typed FeaturePython)
  LinkTransform = true
  LinkedObject = -> _Element032
  _Parent = -> Constraint032
FEATURE [Part::FeaturePython] _Element039  # link proxy (typed FeaturePython)
  Detach = false
  LinkTransform = true
  LinkedObject = -> Part__Feature010 [Edge50]
  _Parent = -> Elements
FEATURE [Part::FeaturePython] _Element040  # link proxy (typed FeaturePython)
  Detach = false
  LinkTransform = true
  LinkedObject = -> Part__Feature010 [Edge28]
  _Parent = -> Elements
FEATURE [App::FeaturePython] Constraint033  label="AxialAlignment017"  # WARN: FeaturePython — macro-defined, semantics opaque (R4)
  Angle = 0
  AnglePitch = 0
  AngleRoll = 0
  Disabled = false
  Group = -> [ElementLink065,ElementLink066]
  LockAngle = false
  Multiply = false
  _ConstraintType = 36
  _Parent = -> Constraints
FEATURE [App::FeaturePython] ElementLink065  label="_Element040"  # link proxy (typed FeaturePython)
  LinkTransform = true
  LinkedObject = -> _Element040
  _Parent = -> Constraint033
FEATURE [App::FeaturePython] ElementLink066  label="_Element004"  # link proxy (typed FeaturePython)
  LinkTransform = true
  LinkedObject = -> _Element004
  _Parent = -> Constraint033
FEATURE [App::FeaturePython] Constraint034  label="PointsCoincident015"  # WARN: FeaturePython — macro-defined, semantics opaque (R4)
  Disabled = false
  Group = -> [ElementLink067,ElementLink068]
  _ConstraintType = 1
  _Parent = -> Constraints
FEATURE [App::FeaturePython] ElementLink067  label="_Element040"  # link proxy (typed FeaturePython)
  LinkTransform = true
  LinkedObject = -> _Element040
  _Parent = -> Constraint034
FEATURE [App::FeaturePython] ElementLink068  label="_Element033"  # link proxy (typed FeaturePython)
  LinkTransform = true
  LinkedObject = -> _Element033
  _Parent = -> Constraint034
note: 1 file-system path scrubbed to <path> (originals preserved in the JSON sidecar)
